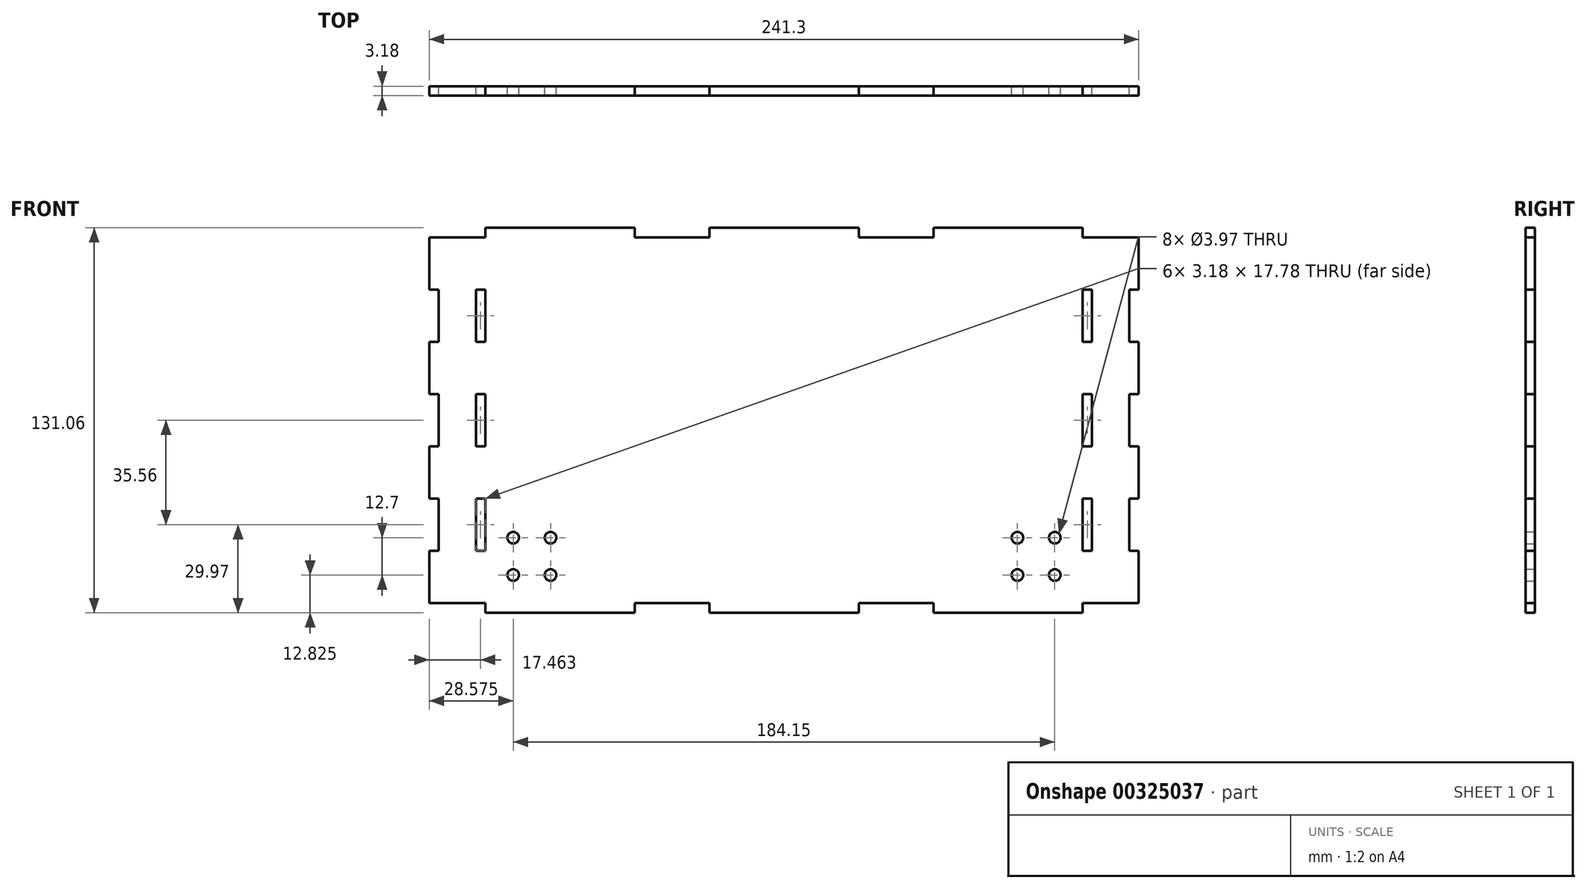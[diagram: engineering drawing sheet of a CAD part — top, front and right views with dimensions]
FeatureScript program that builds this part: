
annotation { "Feature Type Name" : "Feature", "Feature Type Description" : "" }
export const myFeature = defineFeature(function(context is Context, id is Id, definition is map)
    precondition{}
    {
        {
            var Q0;
            Q0=qCreatedBy(makeId("Front.planeOp"),FACE);
            var sketch = newSketch(context, id + "F0", { "sketchPlane" : qUnion([Q0])});
            skLineSegment(sketch, "E0.MirrorCS", {"start": v(-50.8, -65.53) * mm, "end": v(-50.8, -62.23) * mm});
            skLineSegment(sketch, "E1.MirrorCS", {"start": v(25.4, -65.53) * mm, "end": v(25.4, -62.23) * mm});
            skLineSegment(sketch, "E2.MirrorCS", {"start": v(50.8, -65.53) * mm, "end": v(50.8, -62.23) * mm});
            skLineSegment(sketch, "E3.MirrorCS", {"start": v(101.6, -65.53) * mm, "end": v(101.6, -62.23) * mm});
            skLineSegment(sketch, "E4.MirrorCS", {"start": v(-25.4, -65.53) * mm, "end": v(-25.4, -62.23) * mm});
            skLineSegment(sketch, "E5.MirrorCS", {"start": v(101.6, -65.53) * mm, "end": v(50.8, -65.53) * mm});
            skLineSegment(sketch, "E6.MirrorCS", {"start": v(-25.4, -65.53) * mm, "end": v(25.4, -65.53) * mm});
            skLineSegment(sketch, "E7.MirrorCS", {"start": v(-50.8, -65.53) * mm, "end": v(-25.4, -65.53) * mm, "construction": true});
            skLineSegment(sketch, "E8.MirrorCS", {"start": v(-101.6, -65.53) * mm, "end": v(-50.8, -65.53) * mm});
            skLineSegment(sketch, "E9.MirrorCS", {"start": v(-101.6, -65.53) * mm, "end": v(-101.6, -62.23) * mm});
            skLineSegment(sketch, "E10", {"start": v(-120.65, -62.23) * mm, "end": v(-101.6, -62.23) * mm});
            skLineSegment(sketch, "E11.trimOffspring", {"start": v(101.6, -62.23) * mm, "end": v(127, -62.23) * mm});
            skLineSegment(sketch, "E12.trimOffspring", {"start": v(25.4, -62.23) * mm, "end": v(50.8, -62.23) * mm});
            skLineSegment(sketch, "E13.trimOffspring", {"start": v(-50.8, -62.23) * mm, "end": v(-25.4, -62.23) * mm});
            skLineSegment(sketch, "E14", {"start": v(-120.65, 62.23) * mm, "end": v(-120.65, 44.45) * mm});
            skLineSegment(sketch, "E15.MirrorCS", {"start": v(-117.48, 26.67) * mm, "end": v(-117.48, 8.89) * mm, "construction": true});
            skLineSegment(sketch, "E16.MirrorCS", {"start": v(-120.65, -26.67) * mm, "end": v(-120.65, -8.89) * mm});
            skLineSegment(sketch, "E17.MirrorCS", {"start": v(-117.48, 44.45) * mm, "end": v(-117.48, 26.67) * mm});
            skLineSegment(sketch, "E18.MirrorCS", {"start": v(-117.48, -8.9) * mm, "end": v(-117.48, -26.67) * mm, "construction": true});
            skLineSegment(sketch, "E19.MirrorCS", {"start": v(-117.48, 26.67) * mm, "end": v(-120.65, 26.67) * mm});
            skLineSegment(sketch, "E20.MirrorCS", {"start": v(-120.65, 8.89) * mm, "end": v(-117.48, 8.89) * mm});
            skLineSegment(sketch, "E21.MirrorCS", {"start": v(-117.48, 8.89) * mm, "end": v(-117.48, -8.9) * mm});
            skLineSegment(sketch, "E22.MirrorCS", {"start": v(-117.48, -8.89) * mm, "end": v(-120.65, -8.89) * mm});
            skLineSegment(sketch, "E23.MirrorCS", {"start": v(-120.65, -26.67) * mm, "end": v(-117.48, -26.67) * mm});
            skLineSegment(sketch, "E24.MirrorCS", {"start": v(-120.65, 8.89) * mm, "end": v(-120.65, 26.67) * mm});
            skLineSegment(sketch, "E25.MirrorCS", {"start": v(-117.48, -26.67) * mm, "end": v(-117.48, -44.45) * mm});
            skLineSegment(sketch, "E26.MirrorCS", {"start": v(-117.48, -44.45) * mm, "end": v(-120.65, -44.45) * mm});
            skLineSegment(sketch, "E27.MirrorCS", {"start": v(-120.65, 44.45) * mm, "end": v(-117.48, 44.45) * mm});
            skLineSegment(sketch, "E28.trimOffspring", {"start": v(-120.65, 26.67) * mm, "end": v(-120.65, 8.89) * mm});
            skPoint(sketch, "E29.orphan", {"position": v(-120.65, 8.96) * mm});
            skLineSegment(sketch, "E30.trimOffspring", {"start": v(-120.65, -8.89) * mm, "end": v(-120.65, -26.67) * mm});
            skLineSegment(sketch, "E31.trimOffspring", {"start": v(-120.65, -44.45) * mm, "end": v(-120.65, -62.23) * mm});
            skPoint(sketch, "E32", {"position": v(-117.48, 0) * mm});
            skLineSegment(sketch, "E33.MirrorCS", {"start": v(-50.8, 65.53) * mm, "end": v(-25.4, 65.53) * mm, "construction": true});
            skLineSegment(sketch, "E34.MirrorCS", {"start": v(-101.6, 65.53) * mm, "end": v(-101.6, 62.23) * mm});
            skLineSegment(sketch, "E35.MirrorCS", {"start": v(101.6, 62.23) * mm, "end": v(127, 62.23) * mm});
            skLineSegment(sketch, "E36.MirrorCS", {"start": v(25.4, 65.53) * mm, "end": v(25.4, 62.23) * mm});
            skLineSegment(sketch, "E37.MirrorCS", {"start": v(101.6, 65.53) * mm, "end": v(101.6, 62.23) * mm});
            skLineSegment(sketch, "E38.MirrorCS", {"start": v(101.6, 65.53) * mm, "end": v(50.8, 65.53) * mm});
            skLineSegment(sketch, "E39.MirrorCS", {"start": v(-101.6, 65.53) * mm, "end": v(-50.8, 65.53) * mm});
            skLineSegment(sketch, "E40.MirrorCS", {"start": v(-120.65, 62.23) * mm, "end": v(-101.6, 62.23) * mm});
            skLineSegment(sketch, "E41.MirrorCS", {"start": v(25.4, 62.23) * mm, "end": v(50.8, 62.23) * mm});
            skLineSegment(sketch, "E42.MirrorCS", {"start": v(-50.8, 62.23) * mm, "end": v(-25.4, 62.23) * mm});
            skLineSegment(sketch, "E43.MirrorCS", {"start": v(-50.8, 65.53) * mm, "end": v(-50.8, 62.23) * mm});
            skLineSegment(sketch, "E44.MirrorCS", {"start": v(50.8, 65.53) * mm, "end": v(50.8, 62.23) * mm});
            skLineSegment(sketch, "E45.MirrorCS", {"start": v(-25.4, 65.53) * mm, "end": v(-25.4, 62.23) * mm});
            skLineSegment(sketch, "E46.MirrorCS", {"start": v(-25.4, 65.53) * mm, "end": v(25.4, 65.53) * mm});
            skPoint(sketch, "E47", {"position": v(0, 65.53) * mm});
            skLineSegment(sketch, "E48.MirrorCS", {"start": v(117.48, -44.45) * mm, "end": v(120.65, -44.45) * mm});
            skPoint(sketch, "E49.MirrorP", {"position": v(120.65, 8.96) * mm});
            skLineSegment(sketch, "E50.MirrorCS", {"start": v(117.48, 44.45) * mm, "end": v(117.48, 26.67) * mm});
            skLineSegment(sketch, "E51.MirrorCS", {"start": v(117.48, -8.89) * mm, "end": v(120.65, -8.89) * mm});
            skLineSegment(sketch, "E52.MirrorCS", {"start": v(120.65, -26.67) * mm, "end": v(117.48, -26.67) * mm});
            skLineSegment(sketch, "E53.MirrorCS", {"start": v(120.65, 26.67) * mm, "end": v(120.65, 8.89) * mm});
            skLineSegment(sketch, "E54.MirrorCS", {"start": v(120.65, -44.45) * mm, "end": v(120.65, -62.23) * mm});
            skLineSegment(sketch, "E55.MirrorCS", {"start": v(117.48, 26.67) * mm, "end": v(120.65, 26.67) * mm});
            skLineSegment(sketch, "E56.MirrorCS", {"start": v(117.48, -26.67) * mm, "end": v(117.48, -44.45) * mm});
            skLineSegment(sketch, "E57.MirrorCS", {"start": v(120.65, -26.67) * mm, "end": v(120.65, -8.89) * mm});
            skLineSegment(sketch, "E58.MirrorCS", {"start": v(117.48, 8.9) * mm, "end": v(117.48, -8.9) * mm});
            skLineSegment(sketch, "E59.MirrorCS", {"start": v(120.65, 62.23) * mm, "end": v(120.65, 44.45) * mm});
            skLineSegment(sketch, "E60.MirrorCS", {"start": v(120.65, 44.45) * mm, "end": v(117.48, 44.45) * mm});
            skLineSegment(sketch, "E61.MirrorCS", {"start": v(120.65, -8.89) * mm, "end": v(120.65, -26.67) * mm});
            skPoint(sketch, "E62.MirrorP", {"position": v(117.48, 0) * mm});
            skLineSegment(sketch, "E63.MirrorCS", {"start": v(117.48, -8.9) * mm, "end": v(117.48, -26.67) * mm, "construction": true});
            skLineSegment(sketch, "E64.MirrorCS", {"start": v(120.65, 8.89) * mm, "end": v(120.65, 26.67) * mm});
            skLineSegment(sketch, "E65.MirrorCS", {"start": v(117.48, 26.67) * mm, "end": v(117.48, 8.9) * mm, "construction": true});
            skLineSegment(sketch, "E66.MirrorCS", {"start": v(120.65, 8.89) * mm, "end": v(117.48, 8.89) * mm});
            skPoint(sketch, "E67.oppositeSnap0", {"position": v(-119.06, 26.67) * mm});
            skLineSegment(sketch, "E67.bottom", {"start": v(-104.78, 44.45) * mm, "end": v(-101.6, 44.45) * mm});
            skLineSegment(sketch, "E67.top", {"start": v(-104.78, 26.67) * mm, "end": v(-101.6, 26.67) * mm});
            skLineSegment(sketch, "E67.left", {"start": v(-104.78, 44.45) * mm, "end": v(-104.78, 26.67) * mm});
            skLineSegment(sketch, "E67.right", {"start": v(-101.6, 44.45) * mm, "end": v(-101.6, 26.67) * mm});
            skLineSegment(sketch, "E68.bottom", {"start": v(-104.78, 8.89) * mm, "end": v(-101.6, 8.89) * mm});
            skLineSegment(sketch, "E68.top", {"start": v(-104.78, -8.89) * mm, "end": v(-101.6, -8.89) * mm});
            skLineSegment(sketch, "E68.left", {"start": v(-104.78, 8.89) * mm, "end": v(-104.78, -8.89) * mm});
            skLineSegment(sketch, "E68.right", {"start": v(-101.6, 8.89) * mm, "end": v(-101.6, -8.89) * mm});
            skLineSegment(sketch, "E69.bottom", {"start": v(-101.6, -44.45) * mm, "end": v(-104.78, -44.45) * mm});
            skLineSegment(sketch, "E69.top", {"start": v(-101.6, -26.67) * mm, "end": v(-104.78, -26.67) * mm});
            skLineSegment(sketch, "E69.left", {"start": v(-101.6, -44.45) * mm, "end": v(-101.6, -26.67) * mm});
            skLineSegment(sketch, "E69.right", {"start": v(-104.78, -44.45) * mm, "end": v(-104.78, -26.67) * mm});
            skLineSegment(sketch, "E70.MirrorCS", {"start": v(104.78, 8.89) * mm, "end": v(101.6, 8.89) * mm});
            skLineSegment(sketch, "E71.MirrorCS", {"start": v(101.6, -26.67) * mm, "end": v(104.78, -26.67) * mm});
            skLineSegment(sketch, "E72.MirrorCS", {"start": v(104.78, 26.67) * mm, "end": v(101.6, 26.67) * mm});
            skLineSegment(sketch, "E73.MirrorCS", {"start": v(101.6, -44.45) * mm, "end": v(104.78, -44.45) * mm});
            skLineSegment(sketch, "E74.MirrorCS", {"start": v(104.78, 44.45) * mm, "end": v(101.6, 44.45) * mm});
            skLineSegment(sketch, "E75.MirrorCS", {"start": v(104.78, -8.89) * mm, "end": v(101.6, -8.89) * mm});
            skLineSegment(sketch, "E76.MirrorCS", {"start": v(104.78, -44.45) * mm, "end": v(104.78, -26.67) * mm});
            skLineSegment(sketch, "E77.MirrorCS", {"start": v(101.6, 44.45) * mm, "end": v(101.6, 26.67) * mm});
            skLineSegment(sketch, "E78.MirrorCS", {"start": v(101.6, -44.45) * mm, "end": v(101.6, -26.67) * mm});
            skLineSegment(sketch, "E79.MirrorCS", {"start": v(104.78, 44.45) * mm, "end": v(104.78, 26.67) * mm});
            skLineSegment(sketch, "E80.MirrorCS", {"start": v(101.6, 8.89) * mm, "end": v(101.6, -8.89) * mm});
            skLineSegment(sketch, "E81.MirrorCS", {"start": v(104.78, 8.89) * mm, "end": v(104.78, -8.89) * mm});
            skLineSegment(sketch, "E82", {"start": v(-117.48, -44.45) * mm, "end": v(-117.48, -62.23) * mm, "construction": true});
            skCircle(sketch, "E83", {"center": v(-92.08, -52.7) * mm, "radius": 1.98 * mm});
            skCircle(sketch, "E84", {"center": v(-92.08, -40) * mm, "radius": 1.98 * mm});
            skCircle(sketch, "E85", {"center": v(-79.38, -52.7) * mm, "radius": 1.98 * mm});
            skCircle(sketch, "E86", {"center": v(-79.38, -40) * mm, "radius": 1.98 * mm});
            skCircle(sketch, "E87.MirrorC", {"center": v(92.08, -52.7) * mm, "radius": 1.98 * mm});
            skCircle(sketch, "E88.MirrorC", {"center": v(92.08, -40) * mm, "radius": 1.98 * mm});
            skCircle(sketch, "E89.MirrorC", {"center": v(79.38, -52.7) * mm, "radius": 1.98 * mm});
            skCircle(sketch, "E90.MirrorC", {"center": v(79.38, -40) * mm, "radius": 1.98 * mm});
            skSolve(sketch);
        }
        {
            var Q0;
            Q0=makeQuery(id+"F0.imprint","IMPRINT",FACE,{"disambiguationData":[TD([[makeQuery(id+"F0.imprint","IMPRINT",EDGE,{"derivedFrom":sQuery(id+"F0.wireOp",EDGE,"E0.MirrorCS")}),1.0]])]});
            extrude(context, id + "F1", {"entities" : qUnion([Q0]), "depth" : 3.17 * mm});
        }
    });
